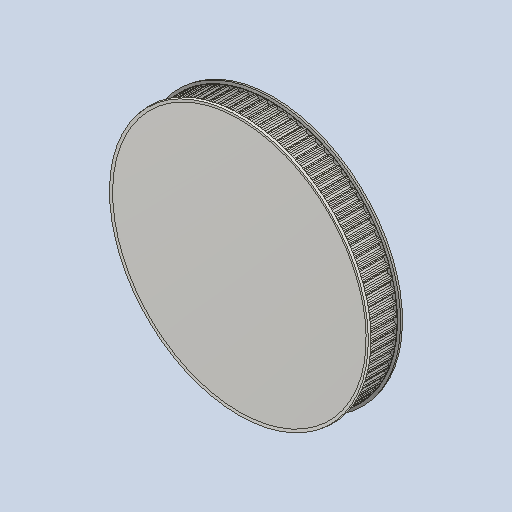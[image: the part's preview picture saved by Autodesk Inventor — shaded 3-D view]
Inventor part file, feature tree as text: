
AUTODESK INVENTOR PART (.ipt)
format: ipt  version: 2024 (Build 280153000, 153)  size: 901,120 bytes
history: native  units: mm (DEFAULTED — no unit token found)
features: other x3, extrude x2, fillet x1, pattern_circular x1
ambient origin geometry x8: Origin, YZ Plane, XZ Plane, XY Plane, X Axis, Y Axis, Z Axis, Center Point
bodies: Solid1 (feature_tree)
feature tree (7):
  other  "Pulley Sketch"
  extrude  "Base Body"  Depth=63.661977mm
  extrude  "Tooth"  Depth=0.3mm
  fillet  "Tooth Fillet"  Radius=0.8382mm
  pattern_circular  "Teeth"  [2 undecoded]
  other  "Left flange"
  other  "Right flange"
note: 2 required parameter values undecoded (feature->parameter linkage not recoverable at this tier; creation-order binding heuristic only, values carry confidence <= 0.55)
